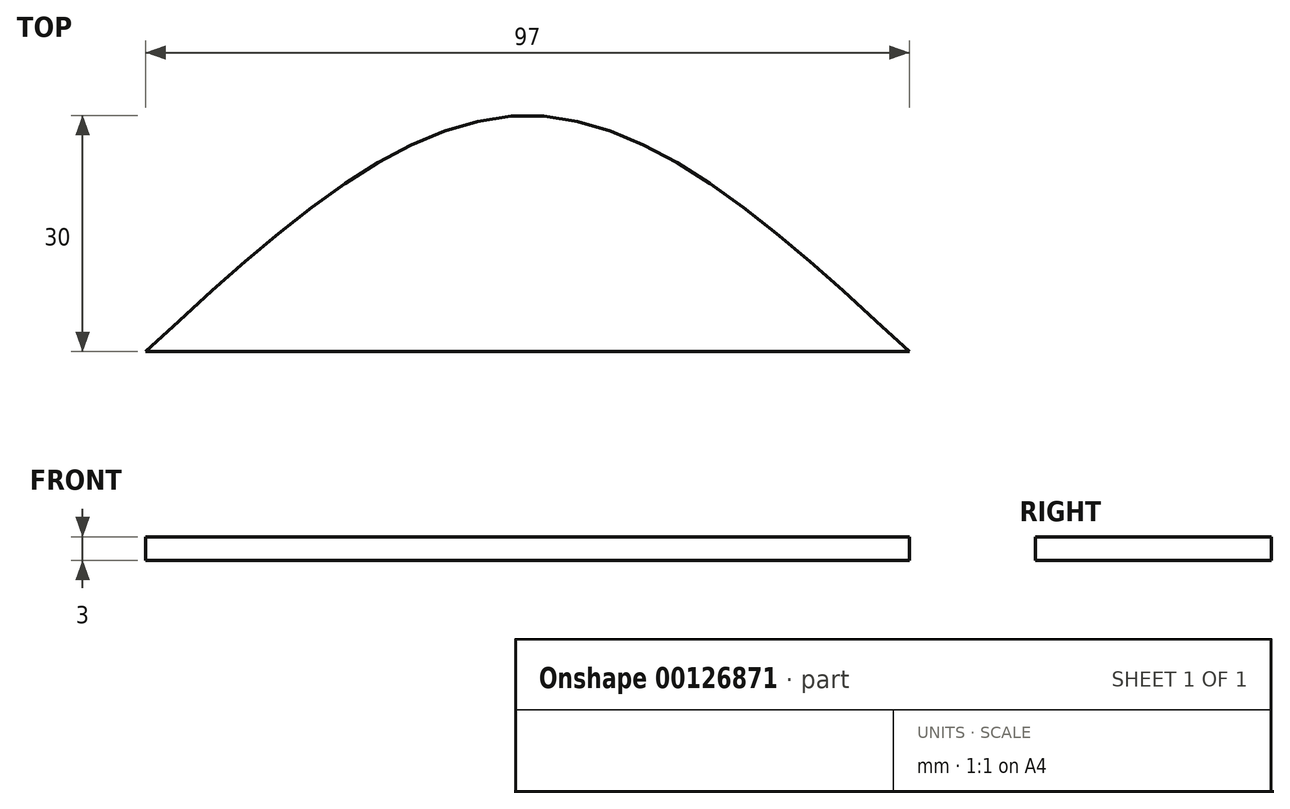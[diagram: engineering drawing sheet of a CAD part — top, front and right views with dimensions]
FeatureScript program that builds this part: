
annotation { "Feature Type Name" : "Feature", "Feature Type Description" : "" }
export const myFeature = defineFeature(function(context is Context, id is Id, definition is map)
    precondition{}
    {
        {
            var Q0;
            Q0=qCreatedBy(makeId("Top.planeOp"),FACE);
            var sketch = newSketch(context, id + "F0", { "sketchPlane" : qUnion([Q0])});
            skFitSpline(sketch, "E0", {"points": [v(-48.5, 0) * mm, v(0, 30) * mm, v(48.5, 0) * mm], "startDerivative": vector(97, 90) * mm, "endDerivative": vector(97, -90) * mm});
            skLineSegment(sketch, "E1.1", {"start": v(40.83, 3) * mm, "end": v(40.83, 3) * mm});
            skFitSpline(sketch, "E2.trimOffspring", {"points": [v(-46.46, -2.2) * mm, v(-42.42, 1.55) * mm, v(-36.39, 7.14) * mm, v(-28.43, 13.83) * mm, v(-22.52, 18.29) * mm, v(-16.7, 22) * mm, v(-11.93, 24.35) * mm, v(-8.19, 25.7) * mm, v(-5.42, 26.44) * mm, v(-3.15, 26.82) * mm, v(-1.34, 26.97) * mm, v(0, 27.01) * mm, v(1.34, 26.97) * mm, v(3.15, 26.82) * mm, v(5.42, 26.44) * mm, v(8.19, 25.7) * mm, v(11.93, 24.35) * mm, v(16.7, 22) * mm, v(22.52, 18.29) * mm, v(28.43, 13.83) * mm, v(36.39, 7.14) * mm, v(42.42, 1.55) * mm, v(46.46, -2.2) * mm]});
            skLineSegment(sketch, "E3", {"start": v(-48.5, 0) * mm, "end": v(48.5, 0) * mm});
            skSolve(sketch);
        }
        {
            var Q0;
            Q0=qSketchRegion(id+"F0",true);
            extrude(context, id + "F1", {"entities" : qUnion([Q0]), "endBound" : BoundingType.SYMMETRIC, "depth" : 3 * mm});
        }
    });
